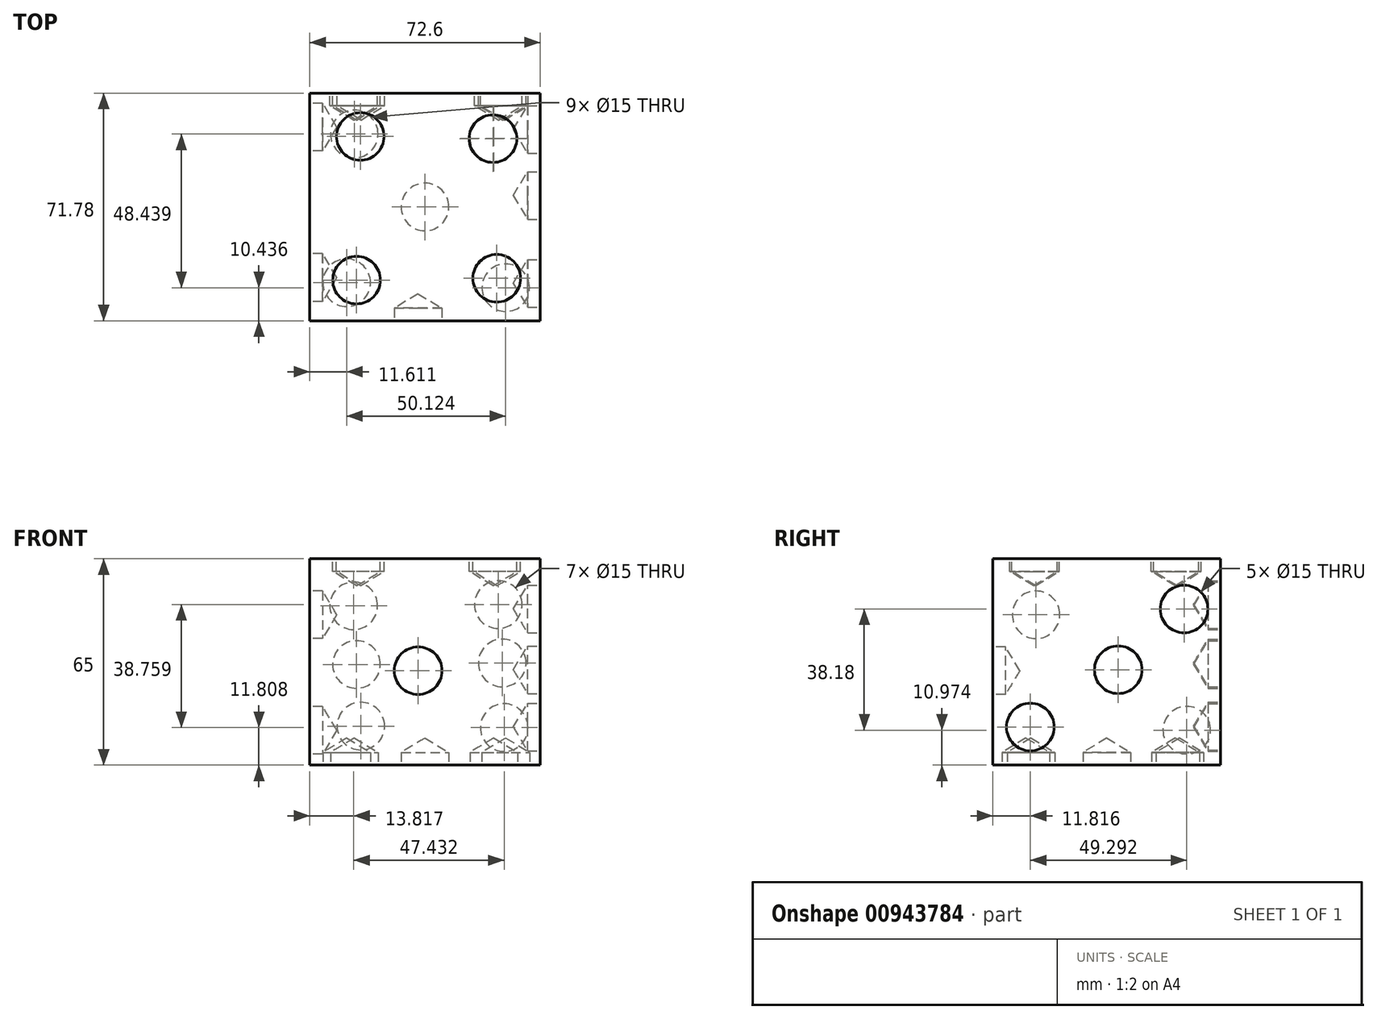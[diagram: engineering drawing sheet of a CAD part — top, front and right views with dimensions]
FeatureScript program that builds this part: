
annotation { "Feature Type Name" : "Feature", "Feature Type Description" : "" }
export const myFeature = defineFeature(function(context is Context, id is Id, definition is map)
    precondition{}
    {
        {
            var Q0;
            Q0=qCreatedBy(makeId("Top.planeOp"),FACE);
            var sketch = newSketch(context, id + "F0", { "sketchPlane" : qUnion([Q0])});
            skLineSegment(sketch, "E0.bottom", {"start": v(36.3, 35.9) * mm, "end": v(-36.3, 35.9) * mm});
            skLineSegment(sketch, "E0.top", {"start": v(36.3, -35.9) * mm, "end": v(-36.3, -35.9) * mm});
            skLineSegment(sketch, "E0.left", {"start": v(36.3, 35.9) * mm, "end": v(36.3, -35.9) * mm});
            skLineSegment(sketch, "E0.right", {"start": v(-36.3, 35.9) * mm, "end": v(-36.3, -35.9) * mm});
            skPoint(sketch, "E0.middle", {"position": v(0, 0) * mm});
            skSolve(sketch);
        }
        {
            var Q0;
            Q0=makeQuery(id+"F0.imprint","IMPRINT",FACE,{"disambiguationData":[TD([[makeQuery(id+"F0.imprint","IMPRINT",EDGE,{"derivedFrom":sQuery(id+"F0.wireOp",EDGE,"E0.bottom")}),1.0]])]});
            extrude(context, id + "F1", {"entities" : qUnion([Q0]), "depth" : 65 * mm, "offsetDistance" : 25.4 * mm});
        }
        {
            var Q0;
            Q0=makeQuery(id+"F1.opExtrude","SWEPT_FACE",FACE,{"disambiguationData":[OSD([sQuery(id+"F0.wireOp",EDGE,"E0.top")])]});
            var sketch = newSketch(context, id + "F2", { "sketchPlane" : qUnion([Q0])});
            skCircle(sketch, "E1", {"center": v(-2.15, 29.73) * mm, "radius": 11.96 * mm});
            skSolve(sketch);
        }
        {
            var Q0;
            Q0=sQuery(id+"F2.wireOp",VERTEX,"E1.center");
            var Q1;
            Q1=makeQuery(id+"F1.opExtrude","SWEPT_BODY",BODY,{"disambiguationData":[OSD([sQuery(id+"F0.wireOp",EDGE,"E0.bottom"),sQuery(id+"F0.wireOp",EDGE,"E0.top"),sQuery(id+"F0.wireOp",EDGE,"E0.left"),sQuery(id+"F0.wireOp",EDGE,"E0.right")])]});
            hole(context, id + "F3", {"style" : HoleStyle.SIMPLE, "endStyle" : HoleEndStyle.BLIND, "holeDiameter" : 15 * mm, "majorDiameter" : 6.35 * mm, "holeDepth" : 4 * mm, "isTappedThrough" : true, "tappedDepth" : 12.7 * mm, "tapClearance" : 3, "locations" : qUnion([Q0]), "scope" : qUnion([Q1])});
        }
        {
            var Q0;
            Q0=makeQuery(id+"F1.opExtrude","SWEPT_FACE",FACE,{"disambiguationData":[OSD([sQuery(id+"F0.wireOp",EDGE,"E0.right")])]});
            var sketch = newSketch(context, id + "F4", { "sketchPlane" : qUnion([Q0])});
            skCircle(sketch, "E2", {"center": v(22.26, 47.35) * mm, "radius": 8.94 * mm});
            skSolve(sketch);
        }
        {
            var Q0;
            Q0=makeQuery(id+"F4.imprint","IMPRINT",FACE,{"disambiguationData":[TD([[makeQuery(id+"F4.imprint","IMPRINT",EDGE,{"derivedFrom":sQuery(id+"F4.wireOp",EDGE,"E2")}),-1.0]])]});
            var sketch = newSketch(context, id + "F5", { "sketchPlane" : qUnion([Q0])});
            skCircle(sketch, "E3", {"center": v(-25.22, 10.97) * mm, "radius": 8.5 * mm});
            skSolve(sketch);
        }
        {
            var Q0;
            Q0=sQuery(id+"F4.wireOp",VERTEX,"E2.center");
            var Q1;
            Q1=makeQuery(id+"F1.opExtrude","SWEPT_BODY",BODY,{"disambiguationData":[OSD([sQuery(id+"F0.wireOp",EDGE,"E0.bottom"),sQuery(id+"F0.wireOp",EDGE,"E0.top"),sQuery(id+"F0.wireOp",EDGE,"E0.left"),sQuery(id+"F0.wireOp",EDGE,"E0.right")])]});
            hole(context, id + "F6", {"style" : HoleStyle.SIMPLE, "endStyle" : HoleEndStyle.BLIND, "holeDiameter" : 15 * mm, "majorDiameter" : 6.35 * mm, "holeDepth" : 4 * mm, "isTappedThrough" : true, "tappedDepth" : 12.7 * mm, "tapClearance" : 3, "locations" : qUnion([Q0]), "scope" : qUnion([Q1])});
        }
        {
            var Q0;
            Q0=sQuery(id+"F5.wireOp",VERTEX,"E3.center");
            var Q1;
            Q1=makeQuery(id+"F1.opExtrude","SWEPT_BODY",BODY,{"disambiguationData":[OSD([sQuery(id+"F0.wireOp",EDGE,"E0.bottom"),sQuery(id+"F0.wireOp",EDGE,"E0.top"),sQuery(id+"F0.wireOp",EDGE,"E0.left"),sQuery(id+"F0.wireOp",EDGE,"E0.right")])]});
            hole(context, id + "F7", {"style" : HoleStyle.SIMPLE, "endStyle" : HoleEndStyle.BLIND, "holeDiameter" : 15 * mm, "majorDiameter" : 6.35 * mm, "holeDepth" : 4 * mm, "isTappedThrough" : true, "tappedDepth" : 12.7 * mm, "tapClearance" : 3, "locations" : qUnion([Q0]), "scope" : qUnion([Q1])});
        }
        {
            var Q0;
            Q0=makeQuery(id+"F1.opExtrude","CAP_FACE",FACE,{"disambiguationData":[OSD([sQuery(id+"F0.wireOp",EDGE,"E0.bottom"),sQuery(id+"F0.wireOp",EDGE,"E0.top"),sQuery(id+"F0.wireOp",EDGE,"E0.left"),sQuery(id+"F0.wireOp",EDGE,"E0.right")])],"isStart":false});
            var sketch = newSketch(context, id + "F8", { "sketchPlane" : qUnion([Q0])});
            skCircle(sketch, "E4", {"center": v(-20.4, 22.2) * mm, "radius": 9.6 * mm});
            skSolve(sketch);
        }
        {
            var Q0;
            Q0=makeQuery(id+"F8.imprint","IMPRINT",FACE,{"disambiguationData":[TD([[makeQuery(id+"F8.imprint","IMPRINT",EDGE,{"derivedFrom":sQuery(id+"F8.wireOp",EDGE,"E4")}),-1.0]])]});
            var sketch = newSketch(context, id + "F9", { "sketchPlane" : qUnion([Q0])});
            skCircle(sketch, "E5", {"center": v(21.43, 21.52) * mm, "radius": 9.68 * mm});
            skSolve(sketch);
        }
        {
            var Q0;
            Q0=makeQuery(id+"F9.imprint","IMPRINT",FACE,{"disambiguationData":[TD([[makeQuery(id+"F9.imprint","IMPRINT",EDGE,{"derivedFrom":sQuery(id+"F9.wireOp",EDGE,"E5")}),-1.0]])]});
            var sketch = newSketch(context, id + "F10", { "sketchPlane" : qUnion([Q0])});
            skCircle(sketch, "E6", {"center": v(-21.58, -23.06) * mm, "radius": 9.87 * mm});
            skSolve(sketch);
        }
        {
            var Q0;
            Q0=makeQuery(id+"F9.imprint","IMPRINT",FACE,{"disambiguationData":[TD([[makeQuery(id+"F9.imprint","IMPRINT",EDGE,{"derivedFrom":sQuery(id+"F9.wireOp",EDGE,"E5")}),-1.0]])]});
            var sketch = newSketch(context, id + "F11", { "sketchPlane" : qUnion([Q0])});
            skCircle(sketch, "E7", {"center": v(22.6, -22.47) * mm, "radius": 9.8 * mm});
            skSolve(sketch);
        }
        {
            var Q0;
            Q0=sQuery(id+"F8.wireOp",VERTEX,"E4.center");
            var Q1;
            Q1=makeQuery(id+"F1.opExtrude","SWEPT_BODY",BODY,{"disambiguationData":[OSD([sQuery(id+"F0.wireOp",EDGE,"E0.bottom"),sQuery(id+"F0.wireOp",EDGE,"E0.top"),sQuery(id+"F0.wireOp",EDGE,"E0.left"),sQuery(id+"F0.wireOp",EDGE,"E0.right")])]});
            hole(context, id + "F12", {"style" : HoleStyle.SIMPLE, "endStyle" : HoleEndStyle.BLIND, "holeDiameter" : 15 * mm, "majorDiameter" : 6.35 * mm, "holeDepth" : 4 * mm, "isTappedThrough" : true, "tappedDepth" : 12.7 * mm, "tapClearance" : 3, "locations" : qUnion([Q0]), "scope" : qUnion([Q1])});
        }
        {
            var Q0;
            Q0=sQuery(id+"F9.wireOp",VERTEX,"E5.center");
            var Q1;
            Q1=makeQuery(id+"F1.opExtrude","SWEPT_BODY",BODY,{"disambiguationData":[OSD([sQuery(id+"F0.wireOp",EDGE,"E0.bottom"),sQuery(id+"F0.wireOp",EDGE,"E0.top"),sQuery(id+"F0.wireOp",EDGE,"E0.left"),sQuery(id+"F0.wireOp",EDGE,"E0.right")])]});
            hole(context, id + "F13", {"style" : HoleStyle.SIMPLE, "endStyle" : HoleEndStyle.BLIND, "holeDiameter" : 15 * mm, "majorDiameter" : 6.35 * mm, "holeDepth" : 4 * mm, "isTappedThrough" : true, "tappedDepth" : 12.7 * mm, "tapClearance" : 3, "locations" : qUnion([Q0]), "scope" : qUnion([Q1])});
        }
        {
            var Q0;
            Q0=sQuery(id+"F10.wireOp",VERTEX,"E6.center");
            var Q1;
            Q1=makeQuery(id+"F1.opExtrude","SWEPT_BODY",BODY,{"disambiguationData":[OSD([sQuery(id+"F0.wireOp",EDGE,"E0.bottom"),sQuery(id+"F0.wireOp",EDGE,"E0.top"),sQuery(id+"F0.wireOp",EDGE,"E0.left"),sQuery(id+"F0.wireOp",EDGE,"E0.right")])]});
            hole(context, id + "F14", {"style" : HoleStyle.SIMPLE, "endStyle" : HoleEndStyle.BLIND, "holeDiameter" : 15 * mm, "majorDiameter" : 6.35 * mm, "holeDepth" : 4 * mm, "isTappedThrough" : true, "tappedDepth" : 12.7 * mm, "tapClearance" : 3, "locations" : qUnion([Q0]), "scope" : qUnion([Q1])});
        }
        {
            var Q0;
            Q0=sQuery(id+"F11.wireOp",VERTEX,"E7.center");
            var Q1;
            Q1=makeQuery(id+"F1.opExtrude","SWEPT_BODY",BODY,{"disambiguationData":[OSD([sQuery(id+"F0.wireOp",EDGE,"E0.bottom"),sQuery(id+"F0.wireOp",EDGE,"E0.top"),sQuery(id+"F0.wireOp",EDGE,"E0.left"),sQuery(id+"F0.wireOp",EDGE,"E0.right")])]});
            hole(context, id + "F15", {"style" : HoleStyle.SIMPLE, "endStyle" : HoleEndStyle.BLIND, "holeDiameter" : 15 * mm, "majorDiameter" : 6.35 * mm, "holeDepth" : 4 * mm, "isTappedThrough" : true, "tappedDepth" : 12.7 * mm, "tapClearance" : 3, "locations" : qUnion([Q0]), "scope" : qUnion([Q1])});
        }
        {
            var Q0;
            Q0=makeQuery(id+"F1.opExtrude","SWEPT_FACE",FACE,{"disambiguationData":[OSD([sQuery(id+"F0.wireOp",EDGE,"E0.bottom")])]});
            var sketch = newSketch(context, id + "F16", { "sketchPlane" : qUnion([Q0])});
            skCircle(sketch, "E8", {"center": v(-23.09, 50.57) * mm, "radius": 7.52 * mm});
            skSolve(sketch);
        }
        {
            var Q0;
            Q0=makeQuery(id+"F16.imprint","IMPRINT",FACE,{"disambiguationData":[TD([[makeQuery(id+"F16.imprint","IMPRINT",EDGE,{"derivedFrom":sQuery(id+"F16.wireOp",EDGE,"E8")}),-1.0]])]});
            var sketch = newSketch(context, id + "F17", { "sketchPlane" : qUnion([Q0])});
            skCircle(sketch, "E9", {"center": v(-24.95, 11.8) * mm, "radius": 7.74 * mm});
            skSolve(sketch);
        }
        {
            var Q0;
            Q0=makeQuery(id+"F16.imprint","IMPRINT",FACE,{"disambiguationData":[TD([[makeQuery(id+"F16.imprint","IMPRINT",EDGE,{"derivedFrom":sQuery(id+"F16.wireOp",EDGE,"E8")}),-1.0]])]});
            var sketch = newSketch(context, id + "F18", { "sketchPlane" : qUnion([Q0])});
            skCircle(sketch, "E10", {"center": v(-24.34, 32.18) * mm, "radius": 7.42 * mm});
            skSolve(sketch);
        }
        {
            var Q0;
            Q0=makeQuery(id+"F17.imprint","IMPRINT",FACE,{"disambiguationData":[TD([[makeQuery(id+"F17.imprint","IMPRINT",EDGE,{"derivedFrom":sQuery(id+"F17.wireOp",EDGE,"E9")}),-1.0]])]});
            var sketch = newSketch(context, id + "F19", { "sketchPlane" : qUnion([Q0])});
            skCircle(sketch, "E11", {"center": v(22.48, 50.19) * mm, "radius": 7.72 * mm});
            skSolve(sketch);
        }
        {
            var Q0;
            Q0=makeQuery(id+"F17.imprint","IMPRINT",FACE,{"disambiguationData":[TD([[makeQuery(id+"F17.imprint","IMPRINT",EDGE,{"derivedFrom":sQuery(id+"F17.wireOp",EDGE,"E9")}),-1.0]])]});
            var sketch = newSketch(context, id + "F20", { "sketchPlane" : qUnion([Q0])});
            skCircle(sketch, "E12", {"center": v(21.6, 31.7) * mm, "radius": 7.84 * mm});
            skSolve(sketch);
        }
        {
            var Q0;
            Q0=makeQuery(id+"F19.imprint","IMPRINT",FACE,{"disambiguationData":[TD([[makeQuery(id+"F19.imprint","IMPRINT",EDGE,{"derivedFrom":sQuery(id+"F19.wireOp",EDGE,"E11")}),-1.0]])]});
            var sketch = newSketch(context, id + "F21", { "sketchPlane" : qUnion([Q0])});
            skCircle(sketch, "E13", {"center": v(20.2, 12.27) * mm, "radius": 7.63 * mm});
            skSolve(sketch);
        }
        {
            var Q0;
            Q0=sQuery(id+"F16.wireOp",VERTEX,"E8.center");
            var Q1;
            Q1=makeQuery(id+"F1.opExtrude","SWEPT_BODY",BODY,{"disambiguationData":[OSD([sQuery(id+"F0.wireOp",EDGE,"E0.bottom"),sQuery(id+"F0.wireOp",EDGE,"E0.top"),sQuery(id+"F0.wireOp",EDGE,"E0.left"),sQuery(id+"F0.wireOp",EDGE,"E0.right")])]});
            hole(context, id + "F22", {"style" : HoleStyle.SIMPLE, "endStyle" : HoleEndStyle.BLIND, "holeDiameter" : 15 * mm, "majorDiameter" : 6.35 * mm, "holeDepth" : 4 * mm, "isTappedThrough" : true, "tappedDepth" : 12.7 * mm, "tapClearance" : 3, "locations" : qUnion([Q0]), "scope" : qUnion([Q1])});
        }
        {
            var Q0;
            Q0=sQuery(id+"F18.wireOp",VERTEX,"E10.center");
            var Q1;
            Q1=makeQuery(id+"F1.opExtrude","SWEPT_BODY",BODY,{"disambiguationData":[OSD([sQuery(id+"F0.wireOp",EDGE,"E0.bottom"),sQuery(id+"F0.wireOp",EDGE,"E0.top"),sQuery(id+"F0.wireOp",EDGE,"E0.left"),sQuery(id+"F0.wireOp",EDGE,"E0.right")])]});
            hole(context, id + "F23", {"style" : HoleStyle.SIMPLE, "endStyle" : HoleEndStyle.BLIND, "holeDiameter" : 15 * mm, "majorDiameter" : 6.35 * mm, "holeDepth" : 4 * mm, "isTappedThrough" : true, "tappedDepth" : 12.7 * mm, "tapClearance" : 3, "locations" : qUnion([Q0]), "scope" : qUnion([Q1])});
        }
        {
            var Q0;
            Q0=sQuery(id+"F17.wireOp",VERTEX,"E9.center");
            var Q1;
            Q1=makeQuery(id+"F1.opExtrude","SWEPT_BODY",BODY,{"disambiguationData":[OSD([sQuery(id+"F0.wireOp",EDGE,"E0.bottom"),sQuery(id+"F0.wireOp",EDGE,"E0.top"),sQuery(id+"F0.wireOp",EDGE,"E0.left"),sQuery(id+"F0.wireOp",EDGE,"E0.right")])]});
            hole(context, id + "F24", {"style" : HoleStyle.SIMPLE, "endStyle" : HoleEndStyle.BLIND, "holeDiameter" : 15 * mm, "majorDiameter" : 6.35 * mm, "holeDepth" : 4 * mm, "isTappedThrough" : true, "tappedDepth" : 12.7 * mm, "tapClearance" : 3, "locations" : qUnion([Q0]), "scope" : qUnion([Q1])});
        }
        {
            var Q0;
            Q0=sQuery(id+"F19.wireOp",VERTEX,"E11.center");
            var Q1;
            Q1=makeQuery(id+"F1.opExtrude","SWEPT_BODY",BODY,{"disambiguationData":[OSD([sQuery(id+"F0.wireOp",EDGE,"E0.bottom"),sQuery(id+"F0.wireOp",EDGE,"E0.top"),sQuery(id+"F0.wireOp",EDGE,"E0.left"),sQuery(id+"F0.wireOp",EDGE,"E0.right")])]});
            hole(context, id + "F25", {"style" : HoleStyle.SIMPLE, "endStyle" : HoleEndStyle.BLIND, "holeDiameter" : 15 * mm, "majorDiameter" : 6.35 * mm, "holeDepth" : 4 * mm, "isTappedThrough" : true, "tappedDepth" : 12.7 * mm, "tapClearance" : 3, "locations" : qUnion([Q0]), "scope" : qUnion([Q1])});
        }
        {
            var Q0;
            Q0=sQuery(id+"F20.wireOp",VERTEX,"E12.center");
            var Q1;
            Q1=makeQuery(id+"F1.opExtrude","SWEPT_BODY",BODY,{"disambiguationData":[OSD([sQuery(id+"F0.wireOp",EDGE,"E0.bottom"),sQuery(id+"F0.wireOp",EDGE,"E0.top"),sQuery(id+"F0.wireOp",EDGE,"E0.left"),sQuery(id+"F0.wireOp",EDGE,"E0.right")])]});
            hole(context, id + "F26", {"style" : HoleStyle.SIMPLE, "endStyle" : HoleEndStyle.BLIND, "holeDiameter" : 15 * mm, "majorDiameter" : 6.35 * mm, "holeDepth" : 4 * mm, "isTappedThrough" : true, "tappedDepth" : 12.7 * mm, "tapClearance" : 3, "locations" : qUnion([Q0]), "scope" : qUnion([Q1])});
        }
        {
            var Q0;
            Q0=sQuery(id+"F21.wireOp",VERTEX,"E13.center");
            var Q1;
            Q1=makeQuery(id+"F1.opExtrude","SWEPT_BODY",BODY,{"disambiguationData":[OSD([sQuery(id+"F0.wireOp",EDGE,"E0.bottom"),sQuery(id+"F0.wireOp",EDGE,"E0.top"),sQuery(id+"F0.wireOp",EDGE,"E0.left"),sQuery(id+"F0.wireOp",EDGE,"E0.right")])]});
            hole(context, id + "F27", {"style" : HoleStyle.SIMPLE, "endStyle" : HoleEndStyle.BLIND, "holeDiameter" : 15 * mm, "majorDiameter" : 6.35 * mm, "holeDepth" : 4 * mm, "isTappedThrough" : true, "tappedDepth" : 12.7 * mm, "tapClearance" : 3, "locations" : qUnion([Q0]), "scope" : qUnion([Q1])});
        }
        {
            var Q0;
            Q0=makeQuery(id+"F1.opExtrude","SWEPT_FACE",FACE,{"disambiguationData":[OSD([sQuery(id+"F0.wireOp",EDGE,"E0.left")])]});
            var sketch = newSketch(context, id + "F28", { "sketchPlane" : qUnion([Q0])});
            skCircle(sketch, "E14", {"center": v(24.37, 49.15) * mm, "radius": 7.14 * mm});
            skSolve(sketch);
        }
        {
            var Q0;
            Q0=makeQuery(id+"F28.imprint","IMPRINT",FACE,{"disambiguationData":[TD([[makeQuery(id+"F28.imprint","IMPRINT",EDGE,{"derivedFrom":sQuery(id+"F28.wireOp",EDGE,"E14")}),-1.0]])]});
            var sketch = newSketch(context, id + "F29", { "sketchPlane" : qUnion([Q0])});
            skCircle(sketch, "E15", {"center": v(3.62, 30.03) * mm, "radius": 7.14 * mm});
            skSolve(sketch);
        }
        {
            var Q0;
            Q0=makeQuery(id+"F29.imprint","IMPRINT",FACE,{"disambiguationData":[TD([[makeQuery(id+"F29.imprint","IMPRINT",EDGE,{"derivedFrom":sQuery(id+"F29.wireOp",EDGE,"E15")}),-1.0]])]});
            var sketch = newSketch(context, id + "F30", { "sketchPlane" : qUnion([Q0])});
            skCircle(sketch, "E16", {"center": v(-24.07, 11.98) * mm, "radius": 7.02 * mm});
            skSolve(sketch);
        }
        {
            var Q0;
            Q0=sQuery(id+"F28.wireOp",VERTEX,"E14.center");
            var Q1;
            Q1=makeQuery(id+"F1.opExtrude","SWEPT_BODY",BODY,{"disambiguationData":[OSD([sQuery(id+"F0.wireOp",EDGE,"E0.bottom"),sQuery(id+"F0.wireOp",EDGE,"E0.top"),sQuery(id+"F0.wireOp",EDGE,"E0.left"),sQuery(id+"F0.wireOp",EDGE,"E0.right")])]});
            hole(context, id + "F31", {"style" : HoleStyle.SIMPLE, "endStyle" : HoleEndStyle.BLIND, "holeDiameter" : 15 * mm, "majorDiameter" : 5 * mm, "holeDepth" : 4 * mm, "isTappedThrough" : true, "tappedDepth" : 12 * mm, "tapClearance" : 3, "locations" : qUnion([Q0]), "scope" : qUnion([Q1])});
        }
        {
            var Q0;
            Q0=sQuery(id+"F29.wireOp",VERTEX,"E15.center");
            var Q1;
            Q1=makeQuery(id+"F1.opExtrude","SWEPT_BODY",BODY,{"disambiguationData":[OSD([sQuery(id+"F0.wireOp",EDGE,"E0.bottom"),sQuery(id+"F0.wireOp",EDGE,"E0.top"),sQuery(id+"F0.wireOp",EDGE,"E0.left"),sQuery(id+"F0.wireOp",EDGE,"E0.right")])]});
            hole(context, id + "F32", {"style" : HoleStyle.SIMPLE, "endStyle" : HoleEndStyle.BLIND, "holeDiameter" : 15 * mm, "majorDiameter" : 5 * mm, "holeDepth" : 4 * mm, "isTappedThrough" : true, "tappedDepth" : 12 * mm, "tapClearance" : 3, "locations" : qUnion([Q0]), "scope" : qUnion([Q1])});
        }
        {
            var Q0;
            Q0=sQuery(id+"F30.wireOp",VERTEX,"E16.center");
            var Q1;
            Q1=makeQuery(id+"F1.opExtrude","SWEPT_BODY",BODY,{"disambiguationData":[OSD([sQuery(id+"F0.wireOp",EDGE,"E0.bottom"),sQuery(id+"F0.wireOp",EDGE,"E0.top"),sQuery(id+"F0.wireOp",EDGE,"E0.left"),sQuery(id+"F0.wireOp",EDGE,"E0.right")])]});
            hole(context, id + "F33", {"style" : HoleStyle.SIMPLE, "endStyle" : HoleEndStyle.BLIND, "holeDiameter" : 15 * mm, "majorDiameter" : 5 * mm, "holeDepth" : 4 * mm, "isTappedThrough" : true, "tappedDepth" : 12 * mm, "tapClearance" : 3, "locations" : qUnion([Q0]), "scope" : qUnion([Q1])});
        }
        {
            var Q0;
            Q0=makeQuery(id+"F1.opExtrude","CAP_FACE",FACE,{"disambiguationData":[OSD([sQuery(id+"F0.wireOp",EDGE,"E0.bottom"),sQuery(id+"F0.wireOp",EDGE,"E0.top"),sQuery(id+"F0.wireOp",EDGE,"E0.left"),sQuery(id+"F0.wireOp",EDGE,"E0.right")])],"isStart":true});
            var sketch = newSketch(context, id + "F34", { "sketchPlane" : qUnion([Q0])});
            skCircle(sketch, "E17", {"center": v(0, 0) * mm, "radius": 6.48 * mm});
            skSolve(sketch);
        }
        {
            var Q0;
            Q0=makeQuery(id+"F34.imprint","IMPRINT",FACE,{"disambiguationData":[TD([[makeQuery(id+"F34.imprint","IMPRINT",EDGE,{"derivedFrom":sQuery(id+"F34.wireOp",EDGE,"E17")}),-1.0]])]});
            var sketch = newSketch(context, id + "F35", { "sketchPlane" : qUnion([Q0])});
            skCircle(sketch, "E18", {"center": v(-24.69, 23.87) * mm, "radius": 6.45 * mm});
            skSolve(sketch);
        }
        {
            var Q0;
            Q0=makeQuery(id+"F34.imprint","IMPRINT",FACE,{"disambiguationData":[TD([[makeQuery(id+"F34.imprint","IMPRINT",EDGE,{"derivedFrom":sQuery(id+"F34.wireOp",EDGE,"E17")}),-1.0]])]});
            var sketch = newSketch(context, id + "F36", { "sketchPlane" : qUnion([Q0])});
            skCircle(sketch, "E19", {"center": v(21.64, -21.67) * mm, "radius": 7.26 * mm});
            skSolve(sketch);
        }
        {
            var Q0;
            Q0=sQuery(id+"F35.wireOp",VERTEX,"E18.center");
            var Q1;
            Q1=makeQuery(id+"F1.opExtrude","SWEPT_BODY",BODY,{"disambiguationData":[OSD([sQuery(id+"F0.wireOp",EDGE,"E0.bottom"),sQuery(id+"F0.wireOp",EDGE,"E0.top"),sQuery(id+"F0.wireOp",EDGE,"E0.left"),sQuery(id+"F0.wireOp",EDGE,"E0.right")])]});
            hole(context, id + "F37", {"style" : HoleStyle.SIMPLE, "endStyle" : HoleEndStyle.BLIND, "holeDiameter" : 15 * mm, "majorDiameter" : 5 * mm, "holeDepth" : 4 * mm, "isTappedThrough" : true, "tappedDepth" : 12 * mm, "tapClearance" : 3, "locations" : qUnion([Q0]), "scope" : qUnion([Q1])});
        }
        {
            var Q0;
            Q0=sQuery(id+"F34.wireOp",VERTEX,"E17.center");
            var Q1;
            Q1=makeQuery(id+"F1.opExtrude","SWEPT_BODY",BODY,{"disambiguationData":[OSD([sQuery(id+"F0.wireOp",EDGE,"E0.bottom"),sQuery(id+"F0.wireOp",EDGE,"E0.top"),sQuery(id+"F0.wireOp",EDGE,"E0.left"),sQuery(id+"F0.wireOp",EDGE,"E0.right")])]});
            hole(context, id + "F38", {"style" : HoleStyle.SIMPLE, "endStyle" : HoleEndStyle.BLIND, "holeDiameter" : 15 * mm, "majorDiameter" : 5 * mm, "holeDepth" : 4 * mm, "isTappedThrough" : true, "tappedDepth" : 12 * mm, "tapClearance" : 3, "locations" : qUnion([Q0]), "scope" : qUnion([Q1])});
        }
        {
            var Q0;
            Q0=makeQuery(id+"F36.imprint","IMPRINT",FACE,{"disambiguationData":[TD([[makeQuery(id+"F36.imprint","IMPRINT",EDGE,{"derivedFrom":sQuery(id+"F36.wireOp",EDGE,"E19")}),-1.0]])]});
            var sketch = newSketch(context, id + "F39", { "sketchPlane" : qUnion([Q0])});
            skCircle(sketch, "E20", {"center": v(-22.28, -22.98) * mm, "radius": 7.03 * mm});
            skSolve(sketch);
        }
        {
            var Q0;
            Q0=makeQuery(id+"F36.imprint","IMPRINT",FACE,{"disambiguationData":[TD([[makeQuery(id+"F36.imprint","IMPRINT",EDGE,{"derivedFrom":sQuery(id+"F36.wireOp",EDGE,"E19")}),-1.0]])]});
            var sketch = newSketch(context, id + "F40", { "sketchPlane" : qUnion([Q0])});
            skCircle(sketch, "E21", {"center": v(25.43, 25.45) * mm, "radius": 7.14 * mm});
            skSolve(sketch);
        }
        {
            var Q0;
            Q0=sQuery(id+"F40.wireOp",VERTEX,"E21.center");
            var Q1;
            Q1=makeQuery(id+"F1.opExtrude","SWEPT_BODY",BODY,{"disambiguationData":[OSD([sQuery(id+"F0.wireOp",EDGE,"E0.bottom"),sQuery(id+"F0.wireOp",EDGE,"E0.top"),sQuery(id+"F0.wireOp",EDGE,"E0.left"),sQuery(id+"F0.wireOp",EDGE,"E0.right")])]});
            hole(context, id + "F41", {"style" : HoleStyle.SIMPLE, "endStyle" : HoleEndStyle.BLIND, "holeDiameter" : 15 * mm, "majorDiameter" : 5 * mm, "holeDepth" : 4 * mm, "isTappedThrough" : true, "tappedDepth" : 12 * mm, "tapClearance" : 3, "locations" : qUnion([Q0]), "scope" : qUnion([Q1])});
        }
        {
            var Q0;
            Q0=sQuery(id+"F39.wireOp",VERTEX,"E20.center");
            var Q1;
            Q1=makeQuery(id+"F1.opExtrude","SWEPT_BODY",BODY,{"disambiguationData":[OSD([sQuery(id+"F0.wireOp",EDGE,"E0.bottom"),sQuery(id+"F0.wireOp",EDGE,"E0.top"),sQuery(id+"F0.wireOp",EDGE,"E0.left"),sQuery(id+"F0.wireOp",EDGE,"E0.right")])]});
            hole(context, id + "F42", {"style" : HoleStyle.SIMPLE, "endStyle" : HoleEndStyle.BLIND, "holeDiameter" : 15 * mm, "majorDiameter" : 5 * mm, "holeDepth" : 4 * mm, "isTappedThrough" : true, "tappedDepth" : 12 * mm, "tapClearance" : 3, "locations" : qUnion([Q0]), "scope" : qUnion([Q1])});
        }
        {
            var Q0;
            Q0=sQuery(id+"F36.wireOp",VERTEX,"E19.center");
            var Q1;
            Q1=makeQuery(id+"F1.opExtrude","SWEPT_BODY",BODY,{"disambiguationData":[OSD([sQuery(id+"F0.wireOp",EDGE,"E0.bottom"),sQuery(id+"F0.wireOp",EDGE,"E0.top"),sQuery(id+"F0.wireOp",EDGE,"E0.left"),sQuery(id+"F0.wireOp",EDGE,"E0.right")])]});
            hole(context, id + "F43", {"style" : HoleStyle.SIMPLE, "endStyle" : HoleEndStyle.BLIND, "holeDiameter" : 15 * mm, "majorDiameter" : 5 * mm, "holeDepth" : 4 * mm, "isTappedThrough" : true, "tappedDepth" : 12 * mm, "tapClearance" : 3, "locations" : qUnion([Q0]), "scope" : qUnion([Q1])});
        }
    });
